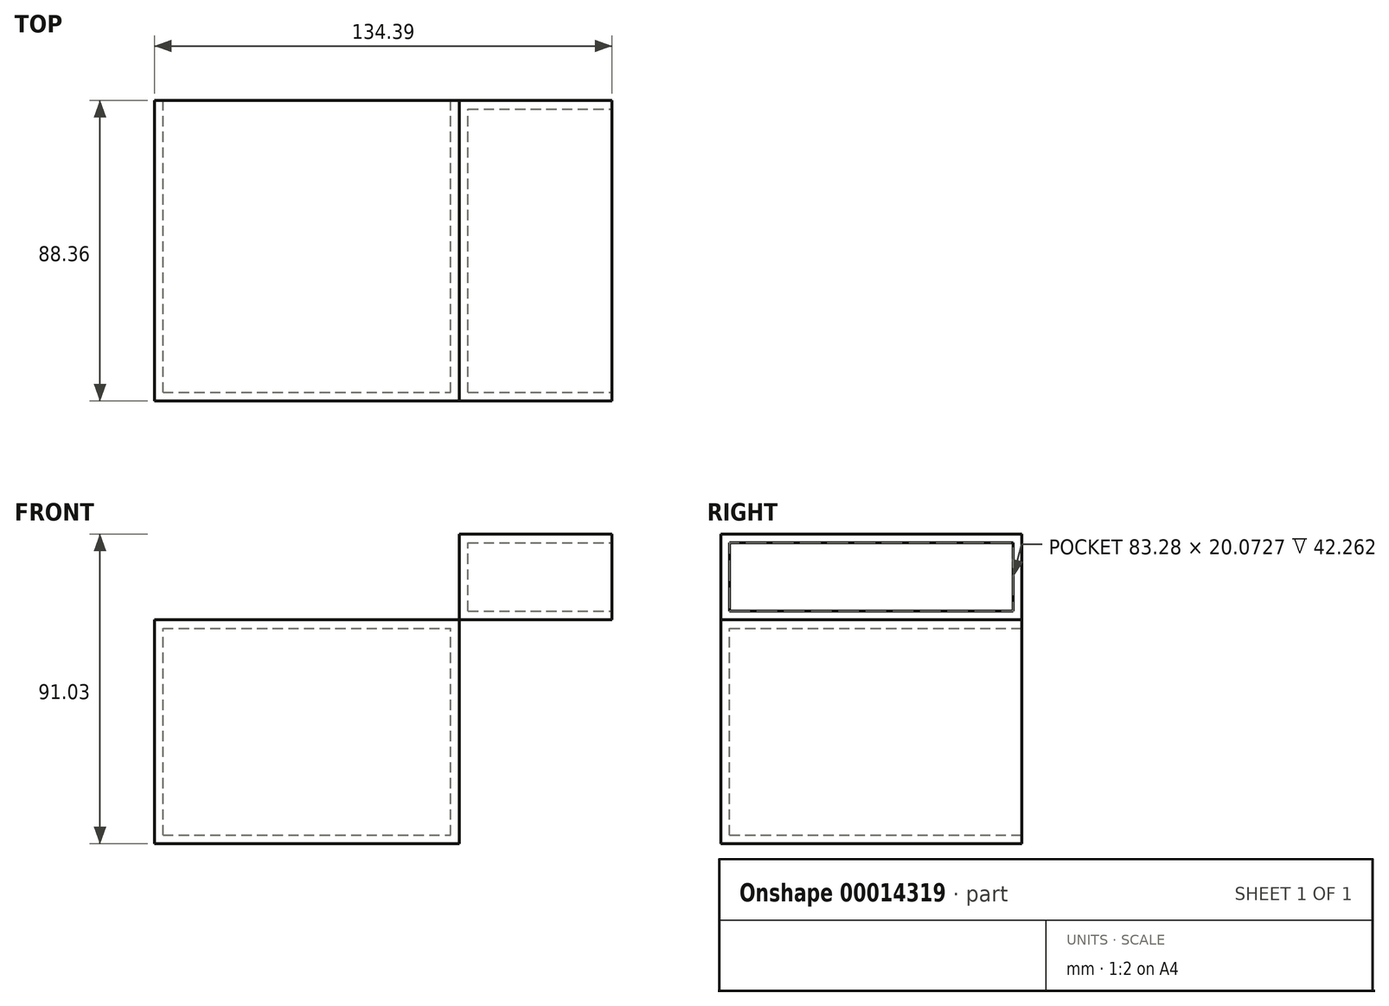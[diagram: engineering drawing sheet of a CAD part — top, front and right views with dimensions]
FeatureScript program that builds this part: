
annotation { "Feature Type Name" : "Feature", "Feature Type Description" : "" }
export const myFeature = defineFeature(function(context is Context, id is Id, definition is map)
    precondition{}
    {
        {
            var Q0;
            Q0=qCreatedBy(makeId("Front.planeOp"),FACE);
            var sketch = newSketch(context, id + "F0", { "sketchPlane" : qUnion([Q0])});
            skLineSegment(sketch, "E0.bottom", {"start": v(-120.04, -35.62) * mm, "end": v(-30.46, -35.62) * mm});
            skLineSegment(sketch, "E0.top", {"start": v(-120.04, 30.26) * mm, "end": v(-30.46, 30.26) * mm});
            skLineSegment(sketch, "E0.left", {"start": v(-120.04, -35.62) * mm, "end": v(-120.04, 30.26) * mm});
            skLineSegment(sketch, "E0.right", {"start": v(-30.46, -35.62) * mm, "end": v(-30.46, 30.26) * mm});
            skLineSegment(sketch, "E1.bottom", {"start": v(-30.46, 30.26) * mm, "end": v(14.35, 30.26) * mm});
            skLineSegment(sketch, "E1.top", {"start": v(-30.46, 55.4) * mm, "end": v(14.35, 55.4) * mm});
            skLineSegment(sketch, "E1.left", {"start": v(-30.46, 30.26) * mm, "end": v(-30.46, 55.4) * mm});
            skLineSegment(sketch, "E1.right", {"start": v(14.35, 30.26) * mm, "end": v(14.35, 55.4) * mm});
            skSolve(sketch);
        }
        {
            var Q0;
            Q0=makeQuery(id+"F0.imprint","IMPRINT",FACE,{"disambiguationData":[TD([[makeQuery(id+"F0.imprint","IMPRINT",EDGE,{"derivedFrom":sQuery(id+"F0.wireOp",EDGE,"E0.bottom")}),1.0]])]});
            var Q1;
            Q1=makeQuery(id+"F0.imprint","IMPRINT",FACE,{"disambiguationData":[TD([[makeQuery(id+"F0.imprint","IMPRINT",EDGE,{"derivedFrom":sQuery(id+"F0.wireOp",EDGE,"E1.bottom")}),1.0]])]});
            extrude(context, id + "F1", {"entities" : qUnion([Q0, Q1]), "depth" : 62.96 * mm, "hasSecondDirection" : true, "secondDirectionOppositeDirection" : true, "secondDirectionDepth" : 25.4 * mm});
        }
        {
            var Q0;
            Q0=makeQuery(id+"F1.opExtrude","SWEPT_FACE",FACE,{"disambiguationData":[OSD([sQuery(id+"F0.wireOp",EDGE,"E1.right")])]});
            var Q1;
            Q1=makeQuery(id+"F1.opExtrude","CAP_FACE",FACE,{"disambiguationData":[OSD([sQuery(id+"F0.wireOp",EDGE,"E0.bottom"),sQuery(id+"F0.wireOp",EDGE,"E0.top"),sQuery(id+"F0.wireOp",EDGE,"E0.left"),sQuery(id+"F0.wireOp",EDGE,"E0.right")])],"isStart":true});
            shell(context, id + "F2", {"entities" : qUnion([Q0, Q1]), "thickness" : 2.54 * mm});
        }
    });
